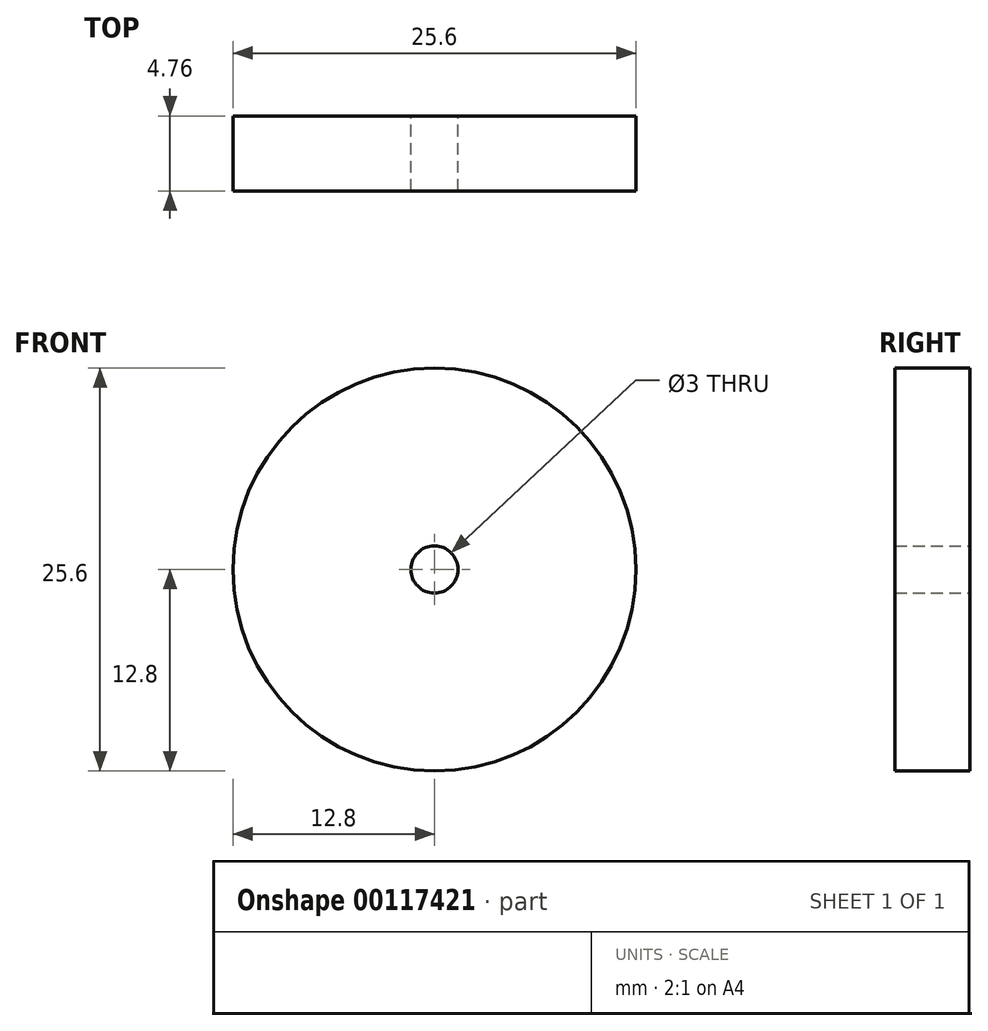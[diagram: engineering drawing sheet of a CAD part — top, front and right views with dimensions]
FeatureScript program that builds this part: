
annotation { "Feature Type Name" : "Feature", "Feature Type Description" : "" }
export const myFeature = defineFeature(function(context is Context, id is Id, definition is map)
    precondition{}
    {
        {
            var Q0;
            Q0=qCreatedBy(makeId("Front.planeOp"),FACE);
            var sketch = newSketch(context, id + "F0", { "sketchPlane" : qUnion([Q0])});
            skCircle(sketch, "E0", {"center": v(0, 0) * mm, "radius": 12.8 * mm});
            skCircle(sketch, "E1", {"center": v(0, 0) * mm, "radius": 1.5 * mm});
            skSolve(sketch);
        }
        {
            var Q0;
            Q0=makeQuery(id+"F0.imprint","IMPRINT",FACE,{"disambiguationData":[TD([[makeQuery(id+"F0.imprint","IMPRINT",EDGE,{"derivedFrom":sQuery(id+"F0.wireOp",EDGE,"E0")}),1.0]])]});
            var Q1;
            Q1=sQuery(id+"F0.wireOp",EDGE,"E1");
            var Q2;
            Q2=sQuery(id+"F0.wireOp",EDGE,"E0");
            extrude(context, id + "F1", {"entities" : qUnion([Q0]), "surfaceEntities" : qUnion([Q1, Q2]), "depth" : 4.76 * mm});
        }
    });
